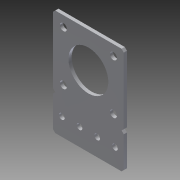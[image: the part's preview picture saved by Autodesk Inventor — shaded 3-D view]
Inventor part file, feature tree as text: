
AUTODESK INVENTOR PART (.ipt)
format: ipt  version: 2014 SP1 (Build 180222100, 222)  size: 162,816 bytes
history: native  units: in
note: dims shown in document units (in); Inventor stores cm internally (conversion verified against a paired STEP export)
features: other x1, extrude x1, imported_body x1, sketch x1
ambient origin geometry x8: Origin, YZ Plane, XZ Plane, XY Plane, X Axis, Y Axis, Z Axis, Center Point
bodies: Body1 (feature_tree)
feature tree (4):
  other  "Cut-Extrude1"
  extrude  "Extrusion1"  Depth=1.0in TaperAngle=0.0deg
  imported_body  "Base1"
  sketch  "Sketch1"  dims[d0=1.125in d1=1.0in d2=0.0in]
